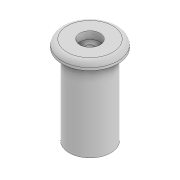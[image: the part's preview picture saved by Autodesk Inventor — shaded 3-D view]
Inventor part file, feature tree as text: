
AUTODESK INVENTOR PART (.ipt)
format: ipt  version: 2022 (Build 260153000, 153)  size: 118,272 bytes
history: native  units: mm
features: extrude x4, sketch x4, fillet x1
ambient origin geometry x8: Origin, YZ Plane, XZ Plane, XY Plane, X Axis, Y Axis, Z Axis, Center Point
bodies: Solid1 (feature_tree)
feature tree (9):
  extrude  "Extrusion1"  Depth=31.8mm TaperAngle=0.0deg
  extrude  "Extrusion2"  Depth=3.0mm TaperAngle=0.0deg
  extrude  "Extrusion3"  Depth=100.0mm TaperAngle=0.0deg
  extrude  "Extrusion4"  Depth=3.0mm TaperAngle=0.0deg
  fillet  "Fillet1"  Radius=2.0mm
  sketch  "Sketch1"  dims[d0=16.4mm d1=31.8mm d2=0.0mm]
  sketch  "Sketch3"  dims[d4=22.0mm d5=3.0mm d6=0.0mm]
  sketch  "Sketch4"  dims[d7=3.2mm d8=100.0mm d9=0.0mm]
  sketch  "Sketch5"  dims[d10=8.0mm d11=3.0mm d12=0.0mm d13=2.0mm]
